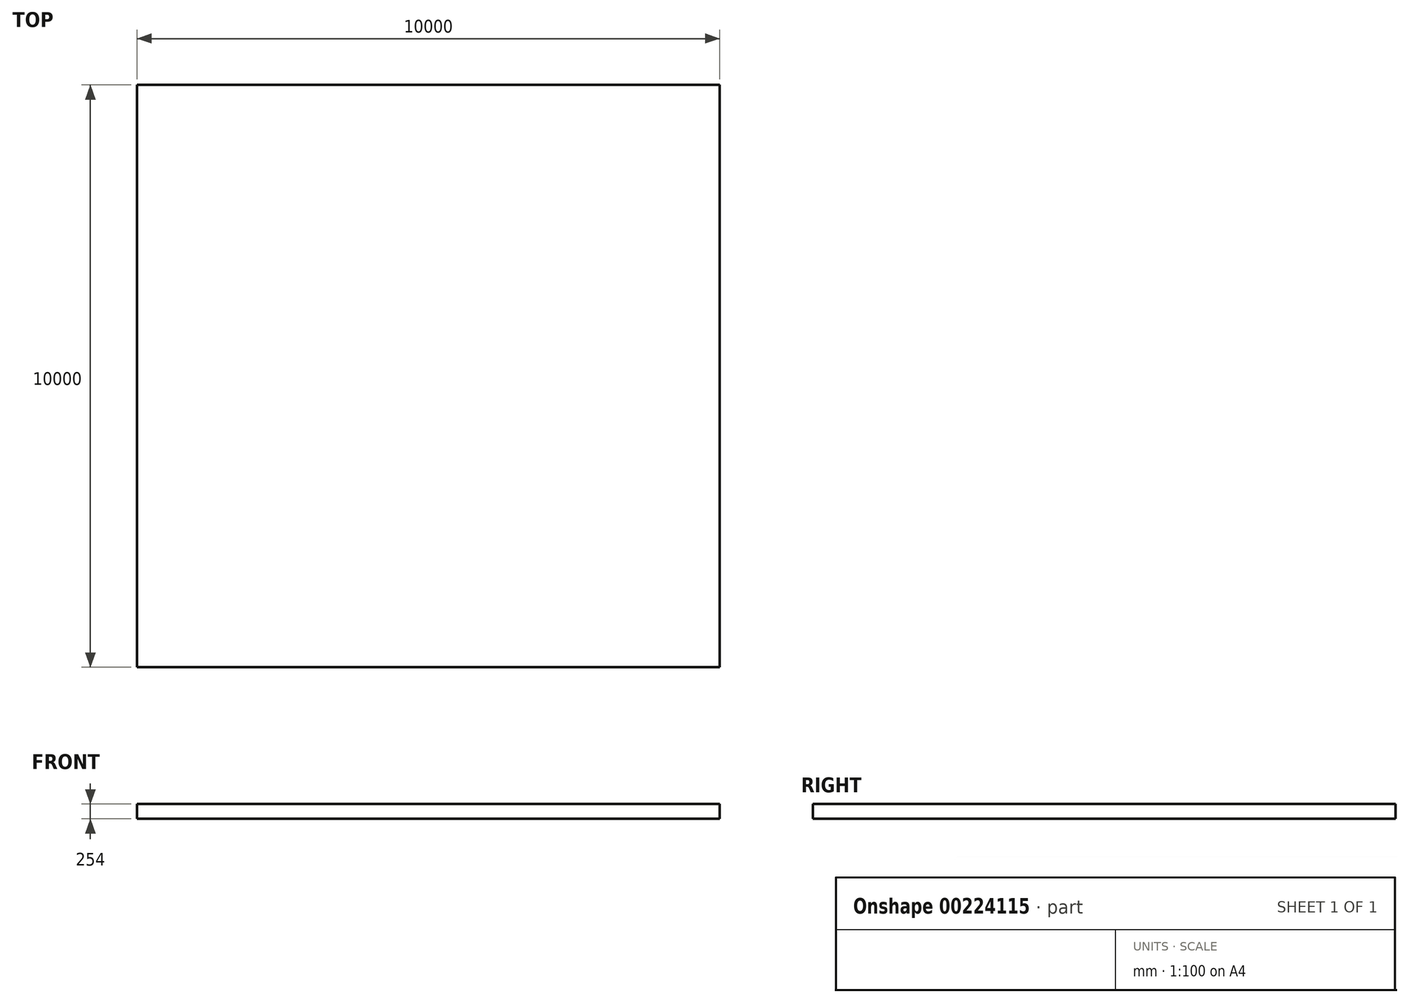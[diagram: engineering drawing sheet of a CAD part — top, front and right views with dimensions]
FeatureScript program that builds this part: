
annotation { "Feature Type Name" : "Feature", "Feature Type Description" : "" }
export const myFeature = defineFeature(function(context is Context, id is Id, definition is map)
    precondition{}
    {
        {
            var Q0;
            Q0=qCreatedBy(makeId("Top.planeOp"),FACE);
            var sketch = newSketch(context, id + "F0", { "sketchPlane" : qUnion([Q0])});
            skLineSegment(sketch, "E0.bottom", {"start": v(-4993.2, 4382.5) * mm, "end": v(5006.8, 4382.5) * mm});
            skLineSegment(sketch, "E0.top", {"start": v(-4993.2, -5617.5) * mm, "end": v(5006.8, -5617.5) * mm});
            skLineSegment(sketch, "E0.left", {"start": v(-4993.2, 4382.5) * mm, "end": v(-4993.2, -5617.5) * mm});
            skLineSegment(sketch, "E0.right", {"start": v(5006.8, 4382.5) * mm, "end": v(5006.8, -5617.5) * mm});
            skSolve(sketch);
        }
        {
            var Q0;
            Q0 = qSketchRegion(id + "F0", true);
            extrude(context, id + "F1", {"entities" : qUnion([Q0]), "depth" : 254 * mm});
        }
    });
